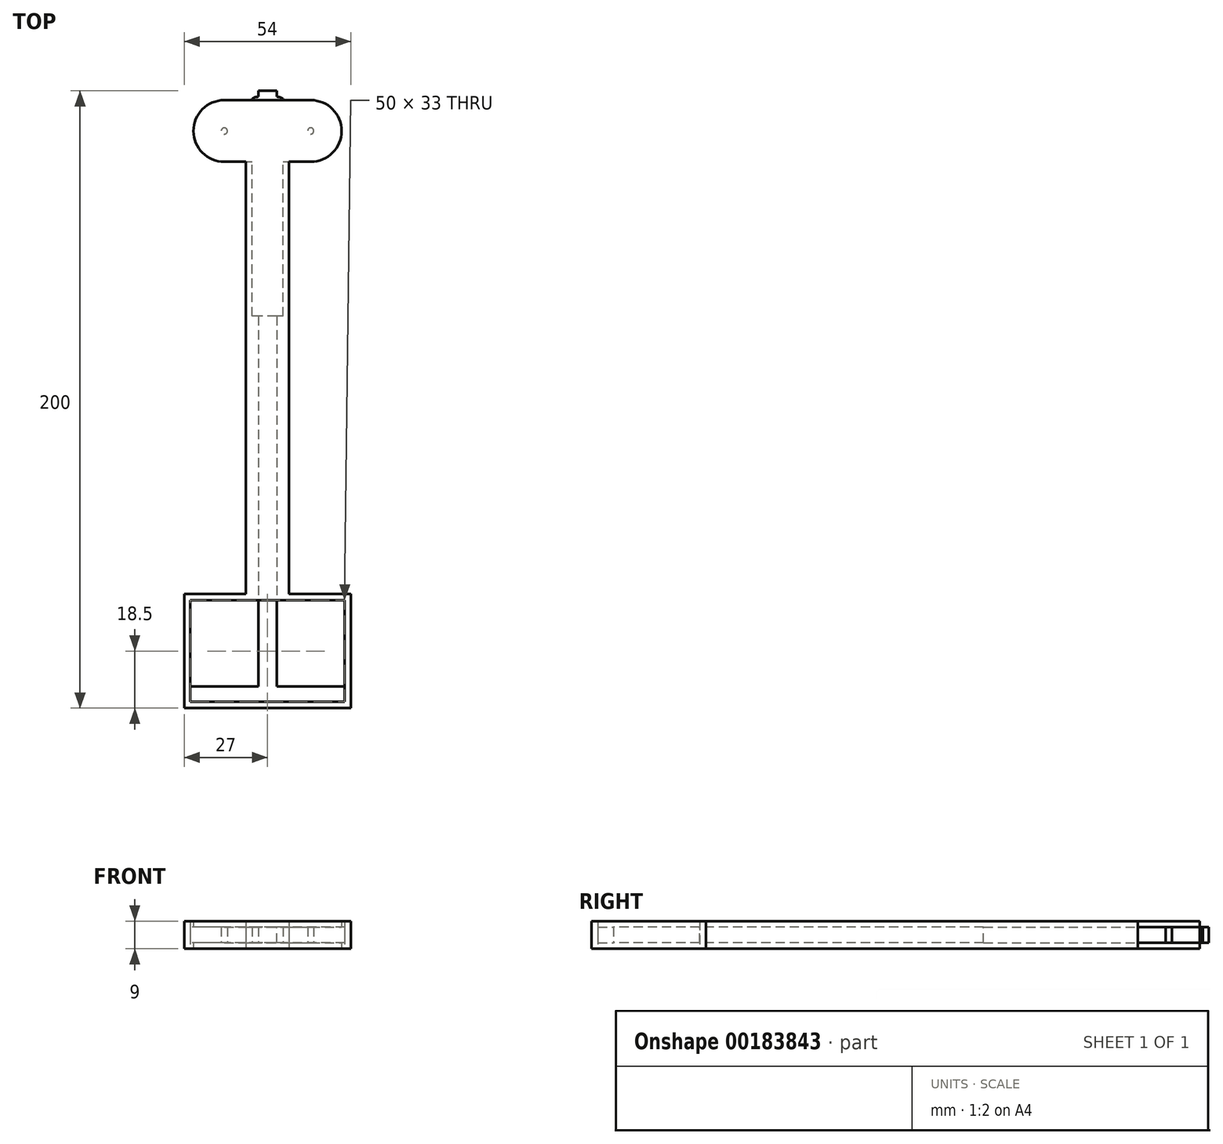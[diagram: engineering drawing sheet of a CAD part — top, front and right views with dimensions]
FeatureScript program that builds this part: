
annotation { "Feature Type Name" : "Feature", "Feature Type Description" : "" }
export const myFeature = defineFeature(function(context is Context, id is Id, definition is map)
    precondition{}
    {
        {
            var Q0;
            Q0=qCreatedBy(makeId("Top.planeOp"),FACE);
            var sketch = newSketch(context, id + "F0", { "sketchPlane" : qUnion([Q0])});
            skLineSegment(sketch, "E0.bottom", {"start": v(3, 13) * mm, "end": v(0, 13) * mm});
            skLineSegment(sketch, "E0.top", {"start": v(3, -180) * mm, "end": v(0, -180) * mm});
            skLineSegment(sketch, "E0.left", {"start": v(3, 13) * mm, "end": v(3, -180) * mm});
            skLineSegment(sketch, "E0.right", {"start": v(0, 13) * mm, "end": v(0, -180) * mm});
            skLineSegment(sketch, "E1", {"start": v(0, 10) * mm, "end": v(3, 10) * mm, "construction": true});
            skArc(sketch, "E2", {"start": v(3, 11.09) * mm, "mid": v(4.04, 10.94) * mm, "end": v(5, 10.5) * mm});
            skLineSegment(sketch, "E3", {"start": v(5, 10.5) * mm, "end": v(5, 10) * mm});
            skArc(sketch, "E4.MirrorCS", {"start": v(3, 8.91) * mm, "mid": v(4.04, 9.06) * mm, "end": v(5, 9.5) * mm});
            skLineSegment(sketch, "E5.MirrorCS", {"start": v(5, 9.5) * mm, "end": v(5, 10) * mm});
            skArc(sketch, "E6.1.0.0", {"start": v(3, 7.89) * mm, "mid": v(4.04, 7.74) * mm, "end": v(5, 7.3) * mm});
            skLineSegment(sketch, "E6.1.0.1", {"start": v(5, 7.3) * mm, "end": v(5, 6.8) * mm});
            skLineSegment(sketch, "E6.1.0.2", {"start": v(5, 6.3) * mm, "end": v(5, 6.8) * mm});
            skArc(sketch, "E6.1.0.3", {"start": v(3, 5.71) * mm, "mid": v(4.04, 5.86) * mm, "end": v(5, 6.3) * mm});
            skArc(sketch, "E6.2.0.0", {"start": v(3, 4.69) * mm, "mid": v(4.04, 4.54) * mm, "end": v(5, 4.1) * mm});
            skLineSegment(sketch, "E6.2.0.1", {"start": v(5, 4.1) * mm, "end": v(5, 3.6) * mm});
            skLineSegment(sketch, "E6.2.0.2", {"start": v(5, 3.1) * mm, "end": v(5, 3.6) * mm});
            skArc(sketch, "E6.2.0.3", {"start": v(3, 2.51) * mm, "mid": v(4.04, 2.66) * mm, "end": v(5, 3.1) * mm});
            skLineSegment(sketch, "E6.direction1", {"start": v(3, 7.39) * mm, "end": v(3, 4.19) * mm, "construction": true});
            skArc(sketch, "E7.0.3.0", {"start": v(3, 1.49) * mm, "mid": v(4.04, 1.34) * mm, "end": v(5, 0.9) * mm});
            skLineSegment(sketch, "E7.4.3.0", {"start": v(5, 0.9) * mm, "end": v(5, 0.4) * mm});
            skLineSegment(sketch, "E7.7.3.0", {"start": v(5, -0.1) * mm, "end": v(5, 0.4) * mm});
            skArc(sketch, "E7.10.3.0", {"start": v(3, -0.69) * mm, "mid": v(4.04, -0.54) * mm, "end": v(5, -0.1) * mm});
            skArc(sketch, "E7.0.4.0", {"start": v(3, -1.71) * mm, "mid": v(4.04, -1.86) * mm, "end": v(5, -2.3) * mm});
            skLineSegment(sketch, "E7.4.4.0", {"start": v(5, -2.3) * mm, "end": v(5, -2.8) * mm});
            skLineSegment(sketch, "E7.7.4.0", {"start": v(5, -3.3) * mm, "end": v(5, -2.8) * mm});
            skArc(sketch, "E7.10.4.0", {"start": v(3, -3.89) * mm, "mid": v(4.04, -3.74) * mm, "end": v(5, -3.3) * mm});
            skArc(sketch, "E7.0.5.0", {"start": v(3, -4.91) * mm, "mid": v(4.04, -5.06) * mm, "end": v(5, -5.5) * mm});
            skLineSegment(sketch, "E7.4.5.0", {"start": v(5, -5.5) * mm, "end": v(5, -6) * mm});
            skLineSegment(sketch, "E7.7.5.0", {"start": v(5, -6.5) * mm, "end": v(5, -6) * mm});
            skArc(sketch, "E7.10.5.0", {"start": v(3, -7.09) * mm, "mid": v(4.04, -6.94) * mm, "end": v(5, -6.5) * mm});
            skArc(sketch, "E7.0.6.0", {"start": v(3, -8.11) * mm, "mid": v(4.04, -8.26) * mm, "end": v(5, -8.7) * mm});
            skLineSegment(sketch, "E7.4.6.0", {"start": v(5, -8.7) * mm, "end": v(5, -9.2) * mm});
            skLineSegment(sketch, "E7.7.6.0", {"start": v(5, -9.7) * mm, "end": v(5, -9.2) * mm});
            skArc(sketch, "E7.10.6.0", {"start": v(3, -10.29) * mm, "mid": v(4.04, -10.14) * mm, "end": v(5, -9.7) * mm});
            skArc(sketch, "E7.0.7.0", {"start": v(3, -11.31) * mm, "mid": v(4.04, -11.46) * mm, "end": v(5, -11.9) * mm});
            skLineSegment(sketch, "E7.4.7.0", {"start": v(5, -11.9) * mm, "end": v(5, -12.4) * mm});
            skLineSegment(sketch, "E7.7.7.0", {"start": v(5, -12.9) * mm, "end": v(5, -12.4) * mm});
            skArc(sketch, "E7.10.7.0", {"start": v(3, -13.49) * mm, "mid": v(4.04, -13.34) * mm, "end": v(5, -12.9) * mm});
            skArc(sketch, "E7.0.8.0", {"start": v(3, -14.51) * mm, "mid": v(4.04, -14.66) * mm, "end": v(5, -15.1) * mm});
            skLineSegment(sketch, "E7.4.8.0", {"start": v(5, -15.1) * mm, "end": v(5, -15.6) * mm});
            skLineSegment(sketch, "E7.7.8.0", {"start": v(5, -16.1) * mm, "end": v(5, -15.6) * mm});
            skArc(sketch, "E7.10.8.0", {"start": v(3, -16.69) * mm, "mid": v(4.04, -16.54) * mm, "end": v(5, -16.1) * mm});
            skArc(sketch, "E7.0.9.0", {"start": v(3, -17.71) * mm, "mid": v(4.04, -17.86) * mm, "end": v(5, -18.3) * mm});
            skLineSegment(sketch, "E7.4.9.0", {"start": v(5, -18.3) * mm, "end": v(5, -18.8) * mm});
            skLineSegment(sketch, "E7.7.9.0", {"start": v(5, -19.3) * mm, "end": v(5, -18.8) * mm});
            skArc(sketch, "E7.10.9.0", {"start": v(3, -19.89) * mm, "mid": v(4.04, -19.74) * mm, "end": v(5, -19.3) * mm});
            skArc(sketch, "E7.0.10.0", {"start": v(3, -20.91) * mm, "mid": v(4.04, -21.06) * mm, "end": v(5, -21.5) * mm});
            skLineSegment(sketch, "E7.4.10.0", {"start": v(5, -21.5) * mm, "end": v(5, -22) * mm});
            skLineSegment(sketch, "E7.7.10.0", {"start": v(5, -22.5) * mm, "end": v(5, -22) * mm});
            skArc(sketch, "E7.10.10.0", {"start": v(3, -23.09) * mm, "mid": v(4.04, -22.94) * mm, "end": v(5, -22.5) * mm});
            skArc(sketch, "E7.0.11.0", {"start": v(3, -24.11) * mm, "mid": v(4.04, -24.26) * mm, "end": v(5, -24.7) * mm});
            skLineSegment(sketch, "E7.4.11.0", {"start": v(5, -24.7) * mm, "end": v(5, -25.2) * mm});
            skLineSegment(sketch, "E7.7.11.0", {"start": v(5, -25.7) * mm, "end": v(5, -25.2) * mm});
            skArc(sketch, "E7.10.11.0", {"start": v(3, -26.29) * mm, "mid": v(4.04, -26.14) * mm, "end": v(5, -25.7) * mm});
            skArc(sketch, "E7.0.12.0", {"start": v(3, -27.31) * mm, "mid": v(4.04, -27.46) * mm, "end": v(5, -27.9) * mm});
            skLineSegment(sketch, "E7.4.12.0", {"start": v(5, -27.9) * mm, "end": v(5, -28.4) * mm});
            skLineSegment(sketch, "E7.7.12.0", {"start": v(5, -28.9) * mm, "end": v(5, -28.4) * mm});
            skArc(sketch, "E7.10.12.0", {"start": v(3, -29.49) * mm, "mid": v(4.04, -29.34) * mm, "end": v(5, -28.9) * mm});
            skArc(sketch, "E7.0.13.0", {"start": v(3, -30.51) * mm, "mid": v(4.04, -30.66) * mm, "end": v(5, -31.1) * mm});
            skLineSegment(sketch, "E7.4.13.0", {"start": v(5, -31.1) * mm, "end": v(5, -31.6) * mm});
            skLineSegment(sketch, "E7.7.13.0", {"start": v(5, -32.1) * mm, "end": v(5, -31.6) * mm});
            skArc(sketch, "E7.10.13.0", {"start": v(3, -32.69) * mm, "mid": v(4.04, -32.54) * mm, "end": v(5, -32.1) * mm});
            skArc(sketch, "E7.0.14.0", {"start": v(3, -33.71) * mm, "mid": v(4.04, -33.86) * mm, "end": v(5, -34.3) * mm});
            skLineSegment(sketch, "E7.4.14.0", {"start": v(5, -34.3) * mm, "end": v(5, -34.8) * mm});
            skLineSegment(sketch, "E7.7.14.0", {"start": v(5, -35.3) * mm, "end": v(5, -34.8) * mm});
            skArc(sketch, "E7.10.14.0", {"start": v(3, -35.89) * mm, "mid": v(4.04, -35.74) * mm, "end": v(5, -35.3) * mm});
            skArc(sketch, "E7.0.15.0", {"start": v(3, -36.91) * mm, "mid": v(4.04, -37.06) * mm, "end": v(5, -37.5) * mm});
            skLineSegment(sketch, "E7.4.15.0", {"start": v(5, -37.5) * mm, "end": v(5, -38) * mm});
            skLineSegment(sketch, "E7.7.15.0", {"start": v(5, -38.5) * mm, "end": v(5, -38) * mm});
            skArc(sketch, "E7.10.15.0", {"start": v(3, -39.09) * mm, "mid": v(4.04, -38.94) * mm, "end": v(5, -38.5) * mm});
            skSolve(sketch);
        }
        {
            var Q0;
            Q0 = qSketchRegion(id + "F0", true);
            extrude(context, id + "F1", {"entities" : qUnion([Q0]), "depth" : 5 * mm});
        }
        {
            var Q0;
            Q0=makeQuery(id+"F1.opExtrude","SWEPT_BODY",BODY,{"disambiguationData":[OSD([sQuery(id+"F0.wireOp",EDGE,"E0.bottom"),sQuery(id+"F0.wireOp",EDGE,"E0.top"),sQuery(id+"F0.wireOp",EDGE,"E0.left"),sQuery(id+"F0.wireOp",EDGE,"E0.right"),sQuery(id+"F0.wireOp",EDGE,"E2"),sQuery(id+"F0.wireOp",EDGE,"E3"),sQuery(id+"F0.wireOp",EDGE,"E4.MirrorCS"),sQuery(id+"F0.wireOp",EDGE,"E5.MirrorCS"),sQuery(id+"F0.wireOp",EDGE,"E6.1.0.0"),sQuery(id+"F0.wireOp",EDGE,"E6.1.0.1"),sQuery(id+"F0.wireOp",EDGE,"E6.1.0.2"),sQuery(id+"F0.wireOp",EDGE,"E6.1.0.3"),sQuery(id+"F0.wireOp",EDGE,"E6.2.0.0"),sQuery(id+"F0.wireOp",EDGE,"E6.2.0.1"),sQuery(id+"F0.wireOp",EDGE,"E6.2.0.2"),sQuery(id+"F0.wireOp",EDGE,"E6.2.0.3"),sQuery(id+"F0.wireOp",EDGE,"E7.0.3.0"),sQuery(id+"F0.wireOp",EDGE,"E7.4.3.0"),sQuery(id+"F0.wireOp",EDGE,"E7.7.3.0"),sQuery(id+"F0.wireOp",EDGE,"E7.10.3.0"),sQuery(id+"F0.wireOp",EDGE,"E7.0.4.0"),sQuery(id+"F0.wireOp",EDGE,"E7.4.4.0"),sQuery(id+"F0.wireOp",EDGE,"E7.7.4.0"),sQuery(id+"F0.wireOp",EDGE,"E7.10.4.0"),sQuery(id+"F0.wireOp",EDGE,"E7.0.5.0"),sQuery(id+"F0.wireOp",EDGE,"E7.4.5.0"),sQuery(id+"F0.wireOp",EDGE,"E7.7.5.0"),sQuery(id+"F0.wireOp",EDGE,"E7.10.5.0"),sQuery(id+"F0.wireOp",EDGE,"E7.0.6.0"),sQuery(id+"F0.wireOp",EDGE,"E7.4.6.0"),sQuery(id+"F0.wireOp",EDGE,"E7.7.6.0"),sQuery(id+"F0.wireOp",EDGE,"E7.10.6.0"),sQuery(id+"F0.wireOp",EDGE,"E7.0.7.0"),sQuery(id+"F0.wireOp",EDGE,"E7.4.7.0"),sQuery(id+"F0.wireOp",EDGE,"E7.7.7.0"),sQuery(id+"F0.wireOp",EDGE,"E7.10.7.0"),sQuery(id+"F0.wireOp",EDGE,"E7.0.8.0"),sQuery(id+"F0.wireOp",EDGE,"E7.4.8.0"),sQuery(id+"F0.wireOp",EDGE,"E7.7.8.0"),sQuery(id+"F0.wireOp",EDGE,"E7.10.8.0"),sQuery(id+"F0.wireOp",EDGE,"E7.0.9.0"),sQuery(id+"F0.wireOp",EDGE,"E7.4.9.0"),sQuery(id+"F0.wireOp",EDGE,"E7.7.9.0"),sQuery(id+"F0.wireOp",EDGE,"E7.10.9.0"),sQuery(id+"F0.wireOp",EDGE,"E7.0.10.0"),sQuery(id+"F0.wireOp",EDGE,"E7.4.10.0"),sQuery(id+"F0.wireOp",EDGE,"E7.7.10.0"),sQuery(id+"F0.wireOp",EDGE,"E7.10.10.0"),sQuery(id+"F0.wireOp",EDGE,"E7.0.11.0"),sQuery(id+"F0.wireOp",EDGE,"E7.4.11.0"),sQuery(id+"F0.wireOp",EDGE,"E7.7.11.0"),sQuery(id+"F0.wireOp",EDGE,"E7.10.11.0"),sQuery(id+"F0.wireOp",EDGE,"E7.0.12.0"),sQuery(id+"F0.wireOp",EDGE,"E7.4.12.0"),sQuery(id+"F0.wireOp",EDGE,"E7.7.12.0"),sQuery(id+"F0.wireOp",EDGE,"E7.10.12.0"),sQuery(id+"F0.wireOp",EDGE,"E7.0.13.0"),sQuery(id+"F0.wireOp",EDGE,"E7.4.13.0"),sQuery(id+"F0.wireOp",EDGE,"E7.7.13.0"),sQuery(id+"F0.wireOp",EDGE,"E7.10.13.0"),sQuery(id+"F0.wireOp",EDGE,"E7.0.14.0"),sQuery(id+"F0.wireOp",EDGE,"E7.4.14.0"),sQuery(id+"F0.wireOp",EDGE,"E7.7.14.0"),sQuery(id+"F0.wireOp",EDGE,"E7.10.14.0"),sQuery(id+"F0.wireOp",EDGE,"E7.0.15.0"),sQuery(id+"F0.wireOp",EDGE,"E7.4.15.0"),sQuery(id+"F0.wireOp",EDGE,"E7.7.15.0"),sQuery(id+"F0.wireOp",EDGE,"E7.10.15.0")])]});
            var Q1;
            Q1=makeQuery(id+"F1.opExtrude","SWEPT_FACE",FACE,{"disambiguationData":[OSD([sQuery(id+"F0.wireOp",EDGE,"E0.right")])]});
            mirror(context, id + "F2", {"operationType" : NewBodyOperationType.ADD, "entities" : qUnion([Q0]), "mirrorPlane" : qUnion([Q1])});
        }
        {
            var Q0;
            {var subQ0=makeQuery(id+"F1.opExtrude","SWEPT_FACE",FACE,{"disambiguationData":[OSD([sQuery(id+"F0.wireOp",EDGE,"E0.top")])]});Q0=makeQuery(id+"F2.boolean.opBoolean","MERGE",FACE,{"derivedFrom":[subQ0,makeQuery(id+"F2.opPattern","COPY",FACE,{"derivedFrom":subQ0,"instanceName":"1"})]});}
            var sketch = newSketch(context, id + "F3", { "sketchPlane" : qUnion([Q0])});
            skLineSegment(sketch, "E8.bottom", {"start": v(25, 5) * mm, "end": v(-25, 5) * mm});
            skLineSegment(sketch, "E8.top", {"start": v(25, 0) * mm, "end": v(-25, 0) * mm});
            skLineSegment(sketch, "E8.left", {"start": v(25, 5) * mm, "end": v(25, 0) * mm});
            skLineSegment(sketch, "E8.right", {"start": v(-25, 5) * mm, "end": v(-25, 0) * mm});
            skPoint(sketch, "E8.middle", {"position": v(0, 2.5) * mm});
            skPoint(sketch, "E8.middle.positionSnap0", {"position": v(-3, 2.5) * mm});
            skPoint(sketch, "E8.centerSnap0", {"position": v(-3, 2.5) * mm});
            skSolve(sketch);
        }
        {
            var Q0;
            Q0 = qSketchRegion(id + "F3", true);
            extrude(context, id + "F4", {"entities" : qUnion([Q0]), "operationType" : NewBodyOperationType.ADD, "depth" : 5 * mm});
        }
        {
            var Q0;
            Q0=qCreatedBy(makeId("Top.planeOp"),FACE);
            var sketch = newSketch(context, id + "F5", { "sketchPlane" : qUnion([Q0])});
            skCircle(sketch, "E9", {"center": v(14, 0) * mm, "radius": 10 * mm});
            skLineSegment(sketch, "E10", {"start": v(14, -10) * mm, "end": v(7, -10) * mm});
            skLineSegment(sketch, "E11", {"start": v(7, -10) * mm, "end": v(7, -150) * mm});
            skLineSegment(sketch, "E12", {"start": v(7, -150) * mm, "end": v(27, -150) * mm});
            skLineSegment(sketch, "E13", {"start": v(27, -150) * mm, "end": v(27, -187) * mm});
            skLineSegment(sketch, "E14", {"start": v(27, -187) * mm, "end": v(0, -187) * mm});
            skLineSegment(sketch, "E15", {"start": v(0, 10) * mm, "end": v(14, 10) * mm});
            skLineSegment(sketch, "E16.MirrorCS", {"start": v(0, 10) * mm, "end": v(-14, 10) * mm});
            skCircle(sketch, "E17.MirrorC", {"center": v(-14, 0) * mm, "radius": 10 * mm});
            skLineSegment(sketch, "E18.MirrorCS", {"start": v(-14, -10) * mm, "end": v(-7, -10) * mm});
            skLineSegment(sketch, "E19.MirrorCS", {"start": v(-7, -10) * mm, "end": v(-7, -150) * mm});
            skLineSegment(sketch, "E20.MirrorCS", {"start": v(-7, -150) * mm, "end": v(-27, -150) * mm});
            skLineSegment(sketch, "E21.MirrorCS", {"start": v(-27, -150) * mm, "end": v(-27, -187) * mm});
            skLineSegment(sketch, "E22.MirrorCS", {"start": v(-27, -187) * mm, "end": v(0, -187) * mm});
            skLineSegment(sketch, "E23.bottom", {"start": v(25, -185) * mm, "end": v(-25, -185) * mm});
            skLineSegment(sketch, "E23.top", {"start": v(25, -152) * mm, "end": v(-25, -152) * mm});
            skLineSegment(sketch, "E23.left", {"start": v(25, -185) * mm, "end": v(25, -152) * mm});
            skLineSegment(sketch, "E23.right", {"start": v(-25, -185) * mm, "end": v(-25, -152) * mm});
            skPoint(sketch, "E23.middle", {"position": v(0, -168.5) * mm});
            skSolve(sketch);
        }
        {
            var Q0;
            Q0 = qSketchRegion(id + "F5", true);
            extrude(context, id + "F6", {"entities" : qUnion([Q0]), "depth" : 7 * mm, "hasSecondDirection" : true, "secondDirectionOppositeDirection" : true, "secondDirectionDepth" : 2 * mm});
        }
        {
            var Q0;
            Q0=makeQuery(id+"F1.opExtrude","SWEPT_BODY",BODY,{"disambiguationData":[OSD([sQuery(id+"F0.wireOp",EDGE,"E0.bottom"),sQuery(id+"F0.wireOp",EDGE,"E0.top"),sQuery(id+"F0.wireOp",EDGE,"E0.left"),sQuery(id+"F0.wireOp",EDGE,"E0.right"),sQuery(id+"F0.wireOp",EDGE,"E2"),sQuery(id+"F0.wireOp",EDGE,"E3"),sQuery(id+"F0.wireOp",EDGE,"E4.MirrorCS"),sQuery(id+"F0.wireOp",EDGE,"E5.MirrorCS"),sQuery(id+"F0.wireOp",EDGE,"E6.1.0.0"),sQuery(id+"F0.wireOp",EDGE,"E6.1.0.1"),sQuery(id+"F0.wireOp",EDGE,"E6.1.0.2"),sQuery(id+"F0.wireOp",EDGE,"E6.1.0.3"),sQuery(id+"F0.wireOp",EDGE,"E6.2.0.0"),sQuery(id+"F0.wireOp",EDGE,"E6.2.0.1"),sQuery(id+"F0.wireOp",EDGE,"E6.2.0.2"),sQuery(id+"F0.wireOp",EDGE,"E6.2.0.3"),sQuery(id+"F0.wireOp",EDGE,"E7.0.3.0"),sQuery(id+"F0.wireOp",EDGE,"E7.4.3.0"),sQuery(id+"F0.wireOp",EDGE,"E7.7.3.0"),sQuery(id+"F0.wireOp",EDGE,"E7.10.3.0"),sQuery(id+"F0.wireOp",EDGE,"E7.0.4.0"),sQuery(id+"F0.wireOp",EDGE,"E7.4.4.0"),sQuery(id+"F0.wireOp",EDGE,"E7.7.4.0"),sQuery(id+"F0.wireOp",EDGE,"E7.10.4.0"),sQuery(id+"F0.wireOp",EDGE,"E7.0.5.0"),sQuery(id+"F0.wireOp",EDGE,"E7.4.5.0"),sQuery(id+"F0.wireOp",EDGE,"E7.7.5.0"),sQuery(id+"F0.wireOp",EDGE,"E7.10.5.0"),sQuery(id+"F0.wireOp",EDGE,"E7.0.6.0"),sQuery(id+"F0.wireOp",EDGE,"E7.4.6.0"),sQuery(id+"F0.wireOp",EDGE,"E7.7.6.0"),sQuery(id+"F0.wireOp",EDGE,"E7.10.6.0"),sQuery(id+"F0.wireOp",EDGE,"E7.0.7.0"),sQuery(id+"F0.wireOp",EDGE,"E7.4.7.0"),sQuery(id+"F0.wireOp",EDGE,"E7.7.7.0"),sQuery(id+"F0.wireOp",EDGE,"E7.10.7.0"),sQuery(id+"F0.wireOp",EDGE,"E7.0.8.0"),sQuery(id+"F0.wireOp",EDGE,"E7.4.8.0"),sQuery(id+"F0.wireOp",EDGE,"E7.7.8.0"),sQuery(id+"F0.wireOp",EDGE,"E7.10.8.0"),sQuery(id+"F0.wireOp",EDGE,"E7.0.9.0"),sQuery(id+"F0.wireOp",EDGE,"E7.4.9.0"),sQuery(id+"F0.wireOp",EDGE,"E7.7.9.0"),sQuery(id+"F0.wireOp",EDGE,"E7.10.9.0"),sQuery(id+"F0.wireOp",EDGE,"E7.0.10.0"),sQuery(id+"F0.wireOp",EDGE,"E7.4.10.0"),sQuery(id+"F0.wireOp",EDGE,"E7.7.10.0"),sQuery(id+"F0.wireOp",EDGE,"E7.10.10.0"),sQuery(id+"F0.wireOp",EDGE,"E7.0.11.0"),sQuery(id+"F0.wireOp",EDGE,"E7.4.11.0"),sQuery(id+"F0.wireOp",EDGE,"E7.7.11.0"),sQuery(id+"F0.wireOp",EDGE,"E7.10.11.0"),sQuery(id+"F0.wireOp",EDGE,"E7.0.12.0"),sQuery(id+"F0.wireOp",EDGE,"E7.4.12.0"),sQuery(id+"F0.wireOp",EDGE,"E7.7.12.0"),sQuery(id+"F0.wireOp",EDGE,"E7.10.12.0"),sQuery(id+"F0.wireOp",EDGE,"E7.0.13.0"),sQuery(id+"F0.wireOp",EDGE,"E7.4.13.0"),sQuery(id+"F0.wireOp",EDGE,"E7.7.13.0"),sQuery(id+"F0.wireOp",EDGE,"E7.10.13.0"),sQuery(id+"F0.wireOp",EDGE,"E7.0.14.0"),sQuery(id+"F0.wireOp",EDGE,"E7.4.14.0"),sQuery(id+"F0.wireOp",EDGE,"E7.7.14.0"),sQuery(id+"F0.wireOp",EDGE,"E7.10.14.0"),sQuery(id+"F0.wireOp",EDGE,"E7.0.15.0"),sQuery(id+"F0.wireOp",EDGE,"E7.4.15.0"),sQuery(id+"F0.wireOp",EDGE,"E7.7.15.0"),sQuery(id+"F0.wireOp",EDGE,"E7.10.15.0")])]});
            var Q1;
            Q1=makeQuery(id+"F6.opExtrude","SWEPT_BODY",BODY,{"disambiguationData":[OSD([sQuery(id+"F5.wireOp",EDGE,"E9"),sQuery(id+"F5.wireOp",EDGE,"E10"),sQuery(id+"F5.wireOp",EDGE,"E11"),sQuery(id+"F5.wireOp",EDGE,"E12"),sQuery(id+"F5.wireOp",EDGE,"E13"),sQuery(id+"F5.wireOp",EDGE,"E14"),sQuery(id+"F5.wireOp",EDGE,"E15"),sQuery(id+"F5.wireOp",EDGE,"E16.MirrorCS"),sQuery(id+"F5.wireOp",EDGE,"E17.MirrorC"),sQuery(id+"F5.wireOp",EDGE,"E18.MirrorCS"),sQuery(id+"F5.wireOp",EDGE,"E19.MirrorCS"),sQuery(id+"F5.wireOp",EDGE,"E20.MirrorCS"),sQuery(id+"F5.wireOp",EDGE,"E21.MirrorCS"),sQuery(id+"F5.wireOp",EDGE,"E22.MirrorCS"),sQuery(id+"F5.wireOp",EDGE,"E23.bottom"),sQuery(id+"F5.wireOp",EDGE,"E23.top"),sQuery(id+"F5.wireOp",EDGE,"E23.left"),sQuery(id+"F5.wireOp",EDGE,"E23.right")])]});
            booleanBodies(context, id + "F7", {"operationType" : BooleanOperationType.SUBTRACTION, "tools" : qUnion([Q0]), "targets" : qUnion([Q1]), "keepTools" : true});
        }
        {
            var Q0;
            Q0=qCreatedBy(makeId("Top.planeOp"),FACE);
            var sketch = newSketch(context, id + "F8", { "sketchPlane" : qUnion([Q0])});
            skArc(sketch, "E24.0", {"start": v(-14, -10) * mm, "mid": v(-24, 0) * mm, "end": v(-14, 10) * mm});
            skLineSegment(sketch, "E25.0", {"start": v(-14, 10) * mm, "end": v(14, 10) * mm});
            skArc(sketch, "E26.0", {"start": v(14, -10) * mm, "mid": v(24, 0) * mm, "end": v(14, 10) * mm});
            skLineSegment(sketch, "E27", {"start": v(-14, -10) * mm, "end": v(14, -10) * mm});
            skSolve(sketch);
        }
        {
            var Q0;
            Q0 = qSketchRegion(id + "F8", true);
            extrude(context, id + "F9", {"entities" : qUnion([Q0]), "operationType" : NewBodyOperationType.REMOVE, "depth" : 5 * mm});
        }
        {
            var Q0;
            {var subQ69=sQuery(id+"F8.wireOp",EDGE,"E27");Q0=makeQuery(id+"F9.boolean.opBoolean","COPY",FACE,{"disambiguationData":[TD([makeQuery(id+"F6.opExtrude","SWEPT_FACE",FACE,{"disambiguationData":[OSD([sQuery(id+"F5.wireOp",EDGE,"E18.MirrorCS")])]})])],"derivedFrom":makeQuery(id+"F9.opExtrude","SWEPT_FACE",FACE,{"disambiguationData":[OSD([subQ69])]})});}
            var sketch = newSketch(context, id + "F10", { "sketchPlane" : qUnion([Q0])});
            skLineSegment(sketch, "E28.bottom", {"start": v(-5, 5) * mm, "end": v(5, 5) * mm});
            skLineSegment(sketch, "E28.top", {"start": v(-5, 0) * mm, "end": v(5, 0) * mm});
            skLineSegment(sketch, "E28.left", {"start": v(-5, 5) * mm, "end": v(-5, 0) * mm});
            skLineSegment(sketch, "E28.right", {"start": v(5, 5) * mm, "end": v(5, 0) * mm});
            skSolve(sketch);
        }
        {
            var Q0;
            Q0 = qSketchRegion(id + "F10", true);
            extrude(context, id + "F11", {"entities" : qUnion([Q0]), "operationType" : NewBodyOperationType.REMOVE, "oppositeDirection" : true, "depth" : 50 * mm});
        }
        {
            var Q0;
            Q0=qCreatedBy(makeId("Top.planeOp"),FACE);
            var sketch = newSketch(context, id + "F12", { "sketchPlane" : qUnion([Q0])});
            skCircle(sketch, "E29", {"center": v(-14, 0) * mm, "radius": 1 * mm});
            skCircle(sketch, "E30", {"center": v(14, 0) * mm, "radius": 1 * mm});
            skSolve(sketch);
        }
        {
            var Q0;
            Q0 = qSketchRegion(id + "F12", true);
            extrude(context, id + "F13", {"entities" : qUnion([Q0]), "operationType" : NewBodyOperationType.ADD, "endBound" : BoundingType.UP_TO_NEXT, "depth" : 25 * mm});
        }
    });
